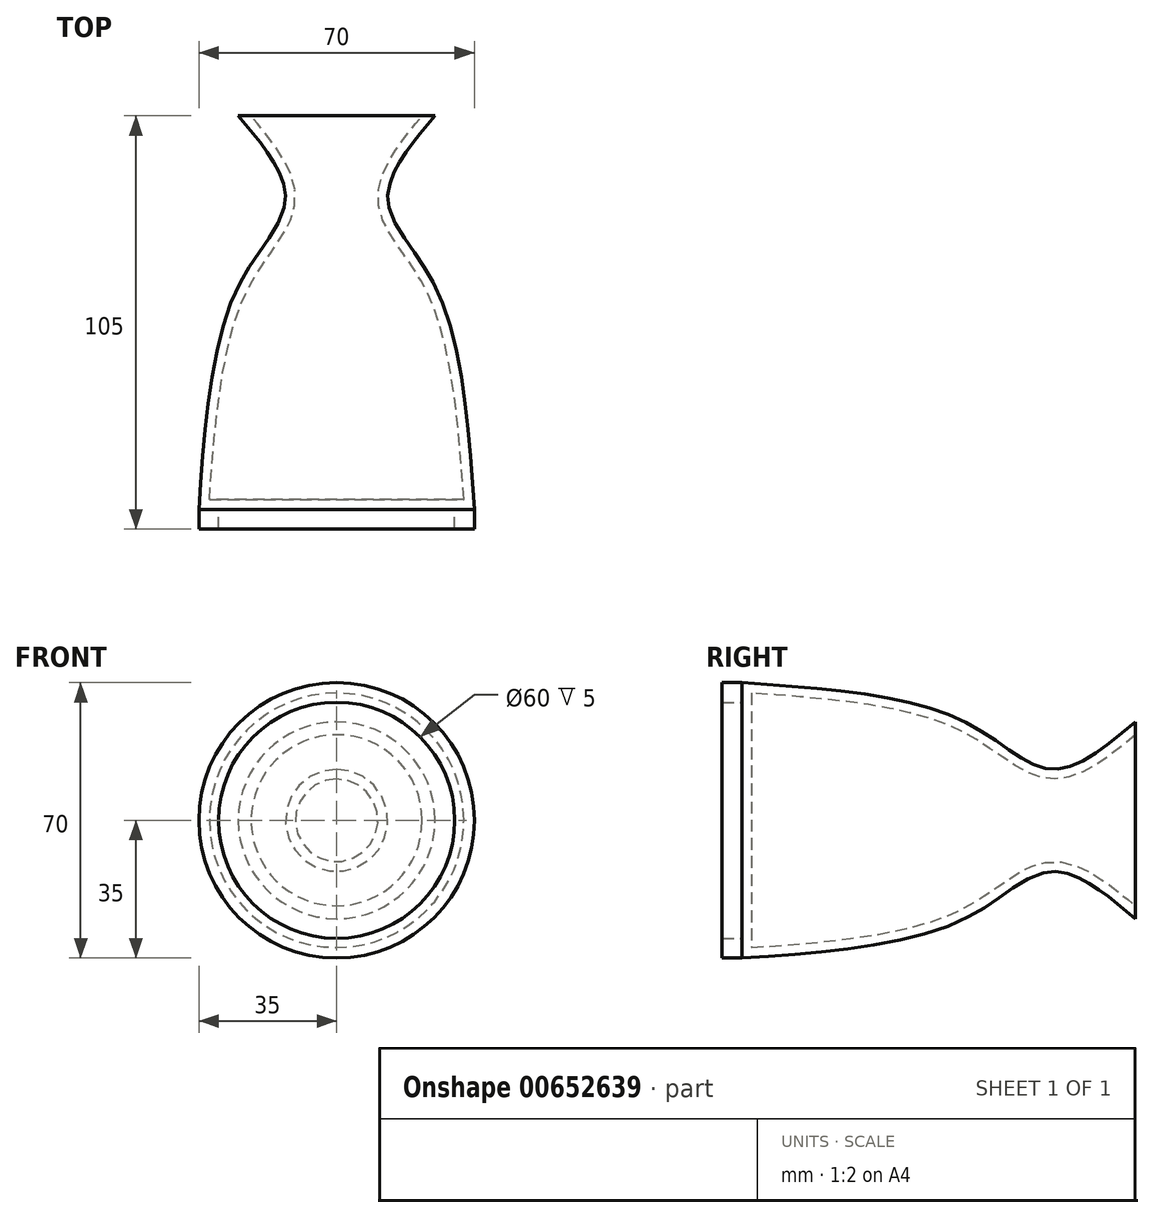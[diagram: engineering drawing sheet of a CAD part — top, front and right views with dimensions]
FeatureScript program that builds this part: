
annotation { "Feature Type Name" : "Feature", "Feature Type Description" : "" }
export const myFeature = defineFeature(function(context is Context, id is Id, definition is map)
    precondition{}
    {
        {
            var Q0;
            Q0=qCreatedBy(makeId("Top.planeOp"),FACE);
            var sketch = newSketch(context, id + "F0", { "sketchPlane" : qUnion([Q0])});
            skLineSegment(sketch, "E0", {"start": v(25, 80.15) * mm, "end": v(0, 80.15) * mm});
            skLineSegment(sketch, "E1", {"start": v(0, 80.15) * mm, "end": v(0, -19.85) * mm});
            skLineSegment(sketch, "E2", {"start": v(0, -19.85) * mm, "end": v(30, -19.85) * mm});
            skLineSegment(sketch, "E3", {"start": v(30, -19.85) * mm, "end": v(30, -24.85) * mm});
            skLineSegment(sketch, "E4", {"start": v(30, -24.85) * mm, "end": v(35, -24.85) * mm});
            skLineSegment(sketch, "E5", {"start": v(35, -24.85) * mm, "end": v(35, -19.85) * mm});
            skFitSpline(sketch, "E6", {"points": [v(25, 80.15) * mm, v(13, 58.94) * mm, v(25, 36.87) * mm, v(35, -19.85) * mm], "startDerivative": vector(-65.75, -77.68) * mm, "endDerivative": vector(10.36, -148) * mm});
            skSolve(sketch);
        }
        {
            var Q0;
            Q0 = qSketchRegion(id + "F0", true);
            var Q1;
            Q1=sQuery(id+"F0.wireOp",EDGE,"E1");
            revolve(context, id + "F1", {"surfaceOperationType" : NewSurfaceOperationType.NEW, "entities" : qUnion([Q0]), "axis" : qUnion([Q1]), "revolveType" : RevolveType.FULL});
        }
        {
            var Q0;
            Q0=makeQuery(id+"F1.opRevolve","SWEPT_FACE",FACE,{"disambiguationData":[OSD([sQuery(id+"F0.wireOp",EDGE,"E0")])]});
            shell(context, id + "F2", {"entities" : qUnion([Q0]), "thickness" : 2.5 * mm});
        }
    });
